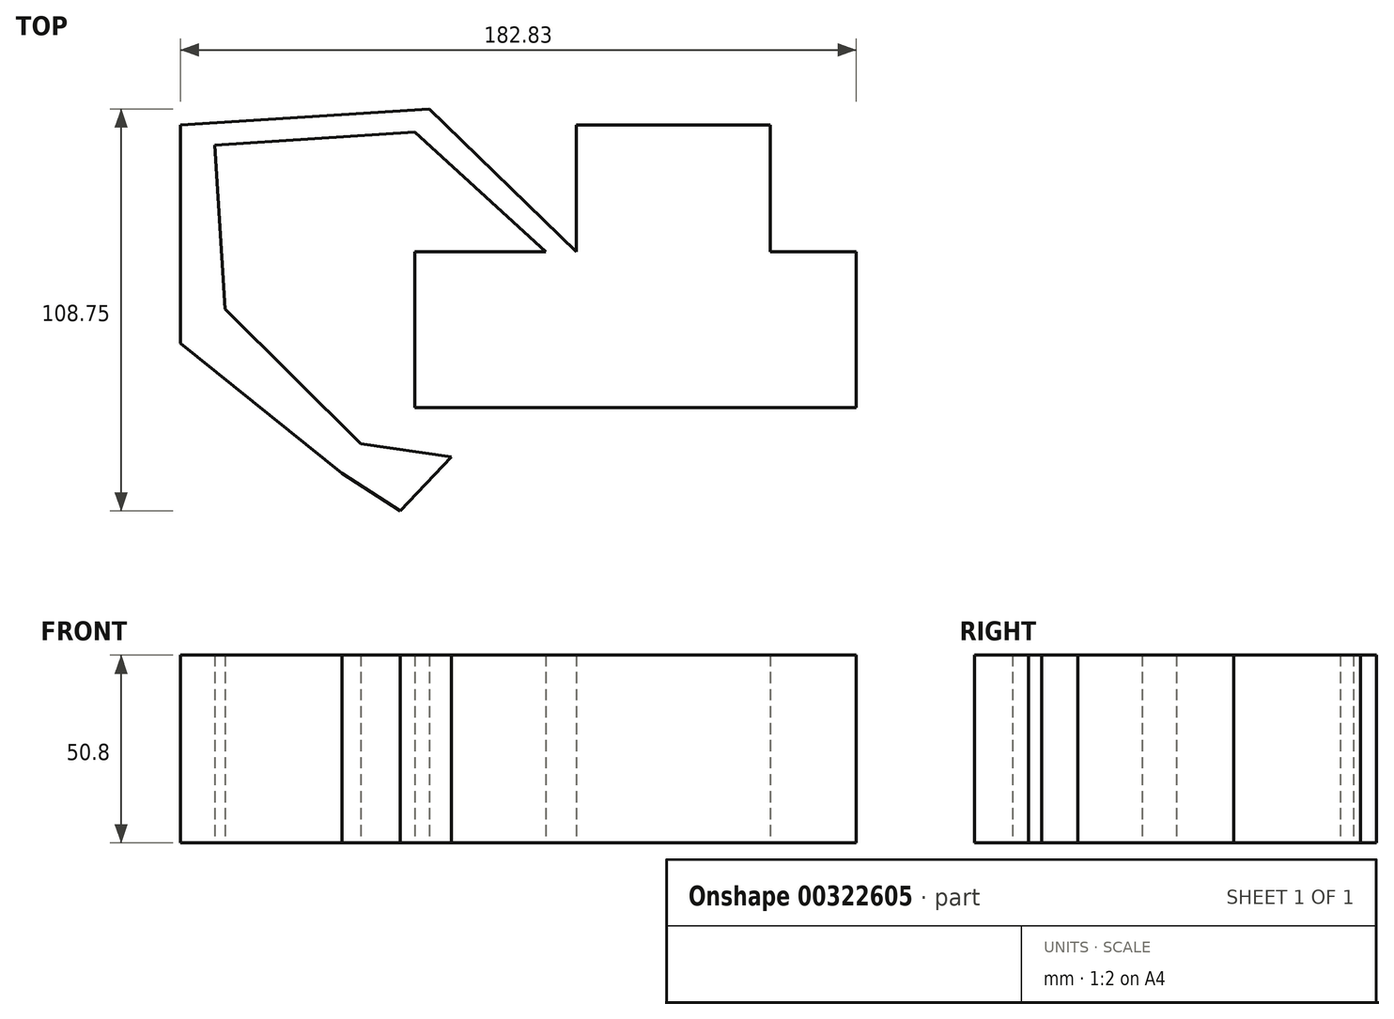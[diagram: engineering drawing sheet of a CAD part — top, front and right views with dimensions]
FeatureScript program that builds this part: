
annotation { "Feature Type Name" : "Feature", "Feature Type Description" : "" }
export const myFeature = defineFeature(function(context is Context, id is Id, definition is map)
    precondition{}
    {
        {
            var Q0;
            Q0=qCreatedBy(makeId("Top.planeOp"),FACE);
            var sketch = newSketch(context, id + "F0", { "sketchPlane" : qUnion([Q0])});
            skLineSegment(sketch, "E0.bottom", {"start": v(-61.47, 15.56) * mm, "end": v(57.92, 15.56) * mm});
            skLineSegment(sketch, "E0.top", {"start": v(-61.47, -26.6) * mm, "end": v(57.92, -26.6) * mm});
            skLineSegment(sketch, "E0.left", {"start": v(-61.47, 15.56) * mm, "end": v(-61.47, -26.6) * mm});
            skLineSegment(sketch, "E0.right", {"start": v(57.92, 15.56) * mm, "end": v(57.92, -26.6) * mm});
            skLineSegment(sketch, "E1.bottom", {"start": v(-17.73, 49.84) * mm, "end": v(34.67, 49.84) * mm});
            skLineSegment(sketch, "E1.top", {"start": v(-17.73, 15.56) * mm, "end": v(34.67, 15.56) * mm});
            skLineSegment(sketch, "E1.left", {"start": v(-17.73, 49.84) * mm, "end": v(-17.73, 15.56) * mm});
            skLineSegment(sketch, "E1.right", {"start": v(34.67, 49.84) * mm, "end": v(34.67, 15.56) * mm});
            skLineSegment(sketch, "E2", {"start": v(-17.73, 15.56) * mm, "end": v(-57.53, 54.18) * mm});
            skLineSegment(sketch, "E3", {"start": v(-57.53, 54.18) * mm, "end": v(-124.9, 49.84) * mm});
            skLineSegment(sketch, "E4", {"start": v(-124.9, 49.84) * mm, "end": v(-124.9, -9.26) * mm});
            skLineSegment(sketch, "E5", {"start": v(-124.9, -9.26) * mm, "end": v(-81.17, -44.33) * mm});
            skLineSegment(sketch, "E6", {"start": v(-26, 15.56) * mm, "end": v(-61.47, 47.87) * mm});
            skLineSegment(sketch, "E7", {"start": v(-61.47, 47.87) * mm, "end": v(-115.6, 44.39) * mm});
            skLineSegment(sketch, "E8", {"start": v(-115.6, 44.39) * mm, "end": v(-112.75, 0) * mm});
            skLineSegment(sketch, "E9", {"start": v(-112.75, 0) * mm, "end": v(-76.05, -36.45) * mm});
            skLineSegment(sketch, "E10", {"start": v(-76.05, -36.45) * mm, "end": v(-51.62, -40) * mm});
            skLineSegment(sketch, "E11", {"start": v(-51.62, -40) * mm, "end": v(-65.4, -54.58) * mm});
            skLineSegment(sketch, "E12", {"start": v(-65.4, -54.58) * mm, "end": v(-81.17, -44.33) * mm});
            skLineSegment(sketch, "E13", {"start": v(-71.02, -37.18) * mm, "end": v(-81.17, -44.33) * mm});
            skLineSegment(sketch, "E14", {"start": v(-51.62, -40) * mm, "end": v(11.03, -31.33) * mm});
            skSolve(sketch);
        }
        {
            var Q0;
            Q0 = qSketchRegion(id + "F0", true);
            extrude(context, id + "F1", {"entities" : qUnion([Q0]), "depth" : 25.4 * mm});
        }
        {
            var Q0;
            Q0=makeQuery(id+"F1.opExtrude","CAP_FACE",FACE,{"disambiguationData":[OSD([sQuery(id+"F0.wireOp",EDGE,"E0.bottom"),sQuery(id+"F0.wireOp",EDGE,"E0.top"),sQuery(id+"F0.wireOp",EDGE,"E0.left"),sQuery(id+"F0.wireOp",EDGE,"E0.right"),sQuery(id+"F0.wireOp",EDGE,"E1.bottom"),sQuery(id+"F0.wireOp",EDGE,"E1.left"),sQuery(id+"F0.wireOp",EDGE,"E1.right"),sQuery(id+"F0.wireOp",EDGE,"E2"),sQuery(id+"F0.wireOp",EDGE,"E3"),sQuery(id+"F0.wireOp",EDGE,"E4"),sQuery(id+"F0.wireOp",EDGE,"E5"),sQuery(id+"F0.wireOp",EDGE,"E6"),sQuery(id+"F0.wireOp",EDGE,"E7"),sQuery(id+"F0.wireOp",EDGE,"E8"),sQuery(id+"F0.wireOp",EDGE,"E9"),sQuery(id+"F0.wireOp",EDGE,"E10"),sQuery(id+"F0.wireOp",EDGE,"E11"),sQuery(id+"F0.wireOp",EDGE,"E12")])],"isStart":true});
            extrude(context, id + "F2", {"entities" : qUnion([Q0]), "operationType" : NewBodyOperationType.ADD, "depth" : 25.4 * mm});
        }
        {
            var Q0;
            Q0=makeQuery(id+"F1.opExtrude","SWEPT_BODY",BODY,{"disambiguationData":[OSD([sQuery(id+"F0.wireOp",EDGE,"E0.bottom"),sQuery(id+"F0.wireOp",EDGE,"E0.top"),sQuery(id+"F0.wireOp",EDGE,"E0.left"),sQuery(id+"F0.wireOp",EDGE,"E0.right"),sQuery(id+"F0.wireOp",EDGE,"E1.bottom"),sQuery(id+"F0.wireOp",EDGE,"E1.left"),sQuery(id+"F0.wireOp",EDGE,"E1.right"),sQuery(id+"F0.wireOp",EDGE,"E2"),sQuery(id+"F0.wireOp",EDGE,"E3"),sQuery(id+"F0.wireOp",EDGE,"E4"),sQuery(id+"F0.wireOp",EDGE,"E5"),sQuery(id+"F0.wireOp",EDGE,"E6"),sQuery(id+"F0.wireOp",EDGE,"E7"),sQuery(id+"F0.wireOp",EDGE,"E8"),sQuery(id+"F0.wireOp",EDGE,"E9"),sQuery(id+"F0.wireOp",EDGE,"E10"),sQuery(id+"F0.wireOp",EDGE,"E11"),sQuery(id+"F0.wireOp",EDGE,"E12")])]});
            var Q1;
            {var subQ0=sQuery(id+"F0.wireOp",EDGE,"E3");Q1=makeQuery(id+"F2.boolean.opBoolean","MERGE",FACE,{"derivedFrom":[makeQuery(id+"F1.opExtrude","SWEPT_FACE",FACE,{"disambiguationData":[OSD([subQ0])]}),makeQuery(id+"F2.opExtrude","SWEPT_FACE",FACE,{"disambiguationData":[OSD([subQ0])]})]});}
            var Q2;
            {var subQ0=sQuery(id+"F0.wireOp",EDGE,"E1.bottom");Q2=makeQuery(id+"F2.boolean.opBoolean","MERGE",FACE,{"derivedFrom":[makeQuery(id+"F1.opExtrude","SWEPT_FACE",FACE,{"disambiguationData":[OSD([subQ0])]}),makeQuery(id+"F2.opExtrude","SWEPT_FACE",FACE,{"disambiguationData":[OSD([subQ0])]})]});}
            transform(context, id + "F3", {"entities" : qUnion([Q0]), "transformType" : TransformType.TRANSLATION_DISTANCE, "transformDirection" : qUnion([Q1, Q2]), "distance" : 25.4 * mm, "oppositeDirection" : true, "makeCopy" : false});
        }
    });
